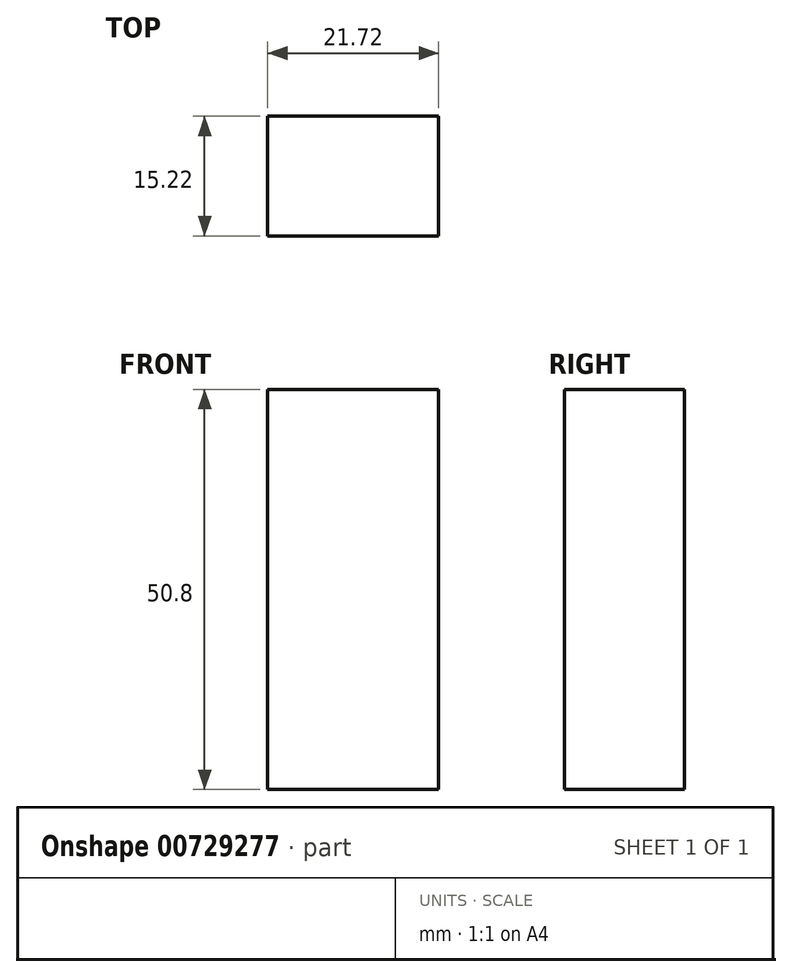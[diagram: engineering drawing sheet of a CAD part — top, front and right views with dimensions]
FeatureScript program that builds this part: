
annotation { "Feature Type Name" : "Feature", "Feature Type Description" : "" }
export const myFeature = defineFeature(function(context is Context, id is Id, definition is map)
    precondition{}
    {
        {
            var Q0;
            Q0=qCreatedBy(makeId("Top.planeOp"),FACE);
            var sketch = newSketch(context, id + "F0", { "sketchPlane" : qUnion([Q0])});
            skLineSegment(sketch, "E0.bottom", {"start": v(-36.77, -44.19) * mm, "end": v(-15.05, -44.19) * mm});
            skLineSegment(sketch, "E0.top", {"start": v(-36.77, -59.4) * mm, "end": v(-15.05, -59.4) * mm});
            skLineSegment(sketch, "E0.left", {"start": v(-36.77, -44.19) * mm, "end": v(-36.77, -59.4) * mm});
            skLineSegment(sketch, "E0.right", {"start": v(-15.05, -44.19) * mm, "end": v(-15.05, -59.4) * mm});
            skSolve(sketch);
        }
        {
            var Q0;
            Q0=makeQuery(id+"F0.imprint","IMPRINT",FACE,{"disambiguationData":[TD([[makeQuery(id+"F0.imprint","IMPRINT",EDGE,{"derivedFrom":sQuery(id+"F0.wireOp",EDGE,"E0.bottom")}),-1.0]])]});
            extrude(context, id + "F1", {"entities" : qUnion([Q0]), "depth" : 50.8 * mm, "offsetDistance" : 25.4 * mm});
        }
    });
